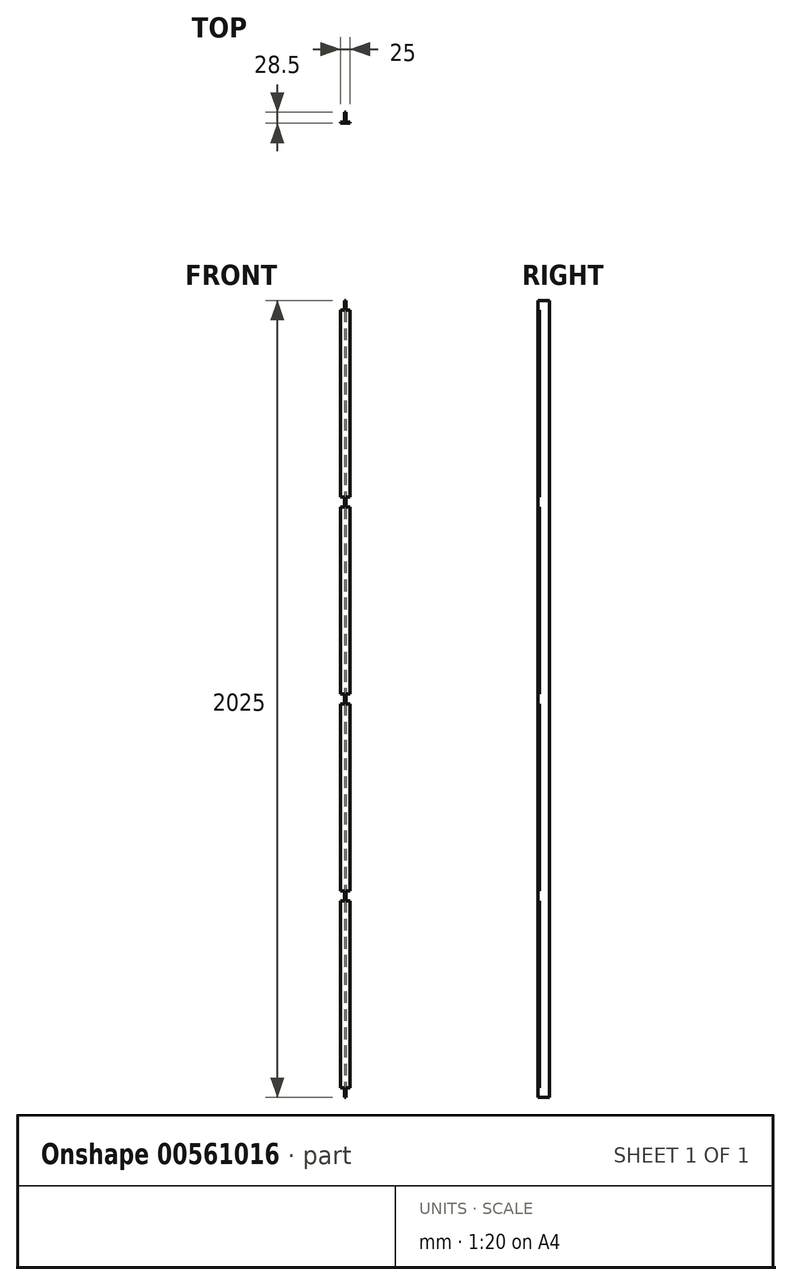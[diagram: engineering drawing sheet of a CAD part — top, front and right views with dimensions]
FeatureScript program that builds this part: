
annotation { "Feature Type Name" : "Feature", "Feature Type Description" : "" }
export const myFeature = defineFeature(function(context is Context, id is Id, definition is map)
    precondition{}
    {
        {
            var Q0;
            Q0=qCreatedBy(makeId("Top.planeOp"),FACE);
            var sketch = newSketch(context, id + "F0", { "sketchPlane" : qUnion([Q0])});
            skLineSegment(sketch, "E0", {"start": v(-14.25, -3.5) * mm, "end": v(10.75, -3.5) * mm});
            skLineSegment(sketch, "E1", {"start": v(10.75, -3.5) * mm, "end": v(10.75, 0) * mm});
            skLineSegment(sketch, "E2", {"start": v(10.75, 0) * mm, "end": v(0, 0) * mm});
            skLineSegment(sketch, "E3", {"start": v(0, 0) * mm, "end": v(0, 25) * mm});
            skLineSegment(sketch, "E4", {"start": v(0, 25) * mm, "end": v(-3.5, 25) * mm});
            skLineSegment(sketch, "E5", {"start": v(-3.5, 25) * mm, "end": v(-3.5, 0) * mm});
            skLineSegment(sketch, "E6", {"start": v(-14.25, 0) * mm, "end": v(-14.25, -3.5) * mm});
            skLineSegment(sketch, "E7", {"start": v(-3.5, 0) * mm, "end": v(-14.25, 0) * mm});
            skSolve(sketch);
        }
        {
            var Q0;
            Q0 = qSketchRegion(id + "F0", true);
            extrude(context, id + "F1", {"entities" : qUnion([Q0]), "depth" : 2025 * mm, "offsetDistance" : 25 * mm});
        }
        {
            var Q0;
            Q0=makeQuery(id+"F1.opExtrude","SWEPT_FACE",FACE,{"disambiguationData":[OSD([sQuery(id+"F0.wireOp",EDGE,"E7")])]});
            var sketch = newSketch(context, id + "F2", { "sketchPlane" : qUnion([Q0])});
            skLineSegment(sketch, "E8.bottom", {"start": v(14.25, 0) * mm, "end": v(3.5, 0) * mm});
            skLineSegment(sketch, "E8.top", {"start": v(14.25, 25) * mm, "end": v(3.5, 25) * mm});
            skLineSegment(sketch, "E8.left", {"start": v(14.25, 0) * mm, "end": v(14.25, 25) * mm});
            skLineSegment(sketch, "E8.right", {"start": v(3.5, 0) * mm, "end": v(3.5, 25) * mm});
            skLineSegment(sketch, "E9.bottom", {"start": v(0, 0) * mm, "end": v(-10.75, 0) * mm});
            skLineSegment(sketch, "E9.top", {"start": v(0, 25) * mm, "end": v(-10.75, 25) * mm});
            skLineSegment(sketch, "E9.left", {"start": v(0, 0) * mm, "end": v(0, 25) * mm});
            skLineSegment(sketch, "E9.right", {"start": v(-10.75, 0) * mm, "end": v(-10.75, 25) * mm});
            skLineSegment(sketch, "E10.bottom", {"start": v(3.5, 2025) * mm, "end": v(14.25, 2025) * mm});
            skLineSegment(sketch, "E10.top", {"start": v(3.5, 2000) * mm, "end": v(14.25, 2000) * mm});
            skLineSegment(sketch, "E10.left", {"start": v(3.5, 2025) * mm, "end": v(3.5, 2000) * mm});
            skLineSegment(sketch, "E10.right", {"start": v(14.25, 2025) * mm, "end": v(14.25, 2000) * mm});
            skLineSegment(sketch, "E11.bottom", {"start": v(0, 2000) * mm, "end": v(-10.75, 2000) * mm});
            skLineSegment(sketch, "E11.top", {"start": v(0, 2025) * mm, "end": v(-10.75, 2025) * mm});
            skLineSegment(sketch, "E11.left", {"start": v(0, 2000) * mm, "end": v(0, 2025) * mm});
            skLineSegment(sketch, "E11.right", {"start": v(-10.75, 2000) * mm, "end": v(-10.75, 2025) * mm});
            skLineSegment(sketch, "E12.bottom", {"start": v(3.5, 1525) * mm, "end": v(14.25, 1525) * mm});
            skLineSegment(sketch, "E12.top", {"start": v(3.5, 1500) * mm, "end": v(14.25, 1500) * mm});
            skLineSegment(sketch, "E12.left", {"start": v(3.5, 1525) * mm, "end": v(3.5, 1500) * mm});
            skLineSegment(sketch, "E12.right", {"start": v(14.25, 1525) * mm, "end": v(14.25, 1500) * mm});
            skLineSegment(sketch, "E13.bottom", {"start": v(0, 1525) * mm, "end": v(-10.75, 1525) * mm});
            skLineSegment(sketch, "E13.top", {"start": v(0, 1500) * mm, "end": v(-10.75, 1500) * mm});
            skLineSegment(sketch, "E13.left", {"start": v(0, 1525) * mm, "end": v(0, 1500) * mm});
            skLineSegment(sketch, "E13.right", {"start": v(-10.75, 1525) * mm, "end": v(-10.75, 1500) * mm});
            skLineSegment(sketch, "E14.bottom", {"start": v(14.25, 1025) * mm, "end": v(3.5, 1025) * mm});
            skLineSegment(sketch, "E14.top", {"start": v(14.25, 1000) * mm, "end": v(3.5, 1000) * mm});
            skLineSegment(sketch, "E14.left", {"start": v(14.25, 1025) * mm, "end": v(14.25, 1000) * mm});
            skLineSegment(sketch, "E14.right", {"start": v(3.5, 1025) * mm, "end": v(3.5, 1000) * mm});
            skLineSegment(sketch, "E15.bottom", {"start": v(0, 1000) * mm, "end": v(-10.75, 1000) * mm});
            skLineSegment(sketch, "E15.top", {"start": v(0, 1025) * mm, "end": v(-10.75, 1025) * mm});
            skLineSegment(sketch, "E15.left", {"start": v(0, 1000) * mm, "end": v(0, 1025) * mm});
            skLineSegment(sketch, "E15.right", {"start": v(-10.75, 1000) * mm, "end": v(-10.75, 1025) * mm});
            skLineSegment(sketch, "E16", {"start": v(-10.75, 1012.5) * mm, "end": v(-10.75, 1512.5) * mm});
            skLineSegment(sketch, "E17", {"start": v(-10.75, 1512.5) * mm, "end": v(-10.75, 2012.5) * mm});
            skLineSegment(sketch, "E18.bottom", {"start": v(3.5, 525) * mm, "end": v(14.25, 525) * mm});
            skLineSegment(sketch, "E18.top", {"start": v(3.5, 500) * mm, "end": v(14.25, 500) * mm});
            skLineSegment(sketch, "E18.left", {"start": v(3.5, 525) * mm, "end": v(3.5, 500) * mm});
            skLineSegment(sketch, "E18.right", {"start": v(14.25, 525) * mm, "end": v(14.25, 500) * mm});
            skLineSegment(sketch, "E19.bottom", {"start": v(0, 525) * mm, "end": v(-10.75, 525) * mm});
            skLineSegment(sketch, "E19.top", {"start": v(0, 500) * mm, "end": v(-10.75, 500) * mm});
            skLineSegment(sketch, "E19.left", {"start": v(0, 525) * mm, "end": v(0, 500) * mm});
            skLineSegment(sketch, "E19.right", {"start": v(-10.75, 525) * mm, "end": v(-10.75, 500) * mm});
            skLineSegment(sketch, "E20", {"start": v(-10.75, 1012.5) * mm, "end": v(-10.75, 512.5) * mm});
            skLineSegment(sketch, "E21", {"start": v(-10.75, 512.5) * mm, "end": v(-10.75, 12.5) * mm});
            skSolve(sketch);
        }
        {
            var Q0;
            Q0 = qSketchRegion(id + "F2", true);
            extrude(context, id + "F3", {"entities" : qUnion([Q0]), "operationType" : NewBodyOperationType.REMOVE, "endBound" : BoundingType.THROUGH_ALL, "oppositeDirection" : true, "depth" : 25 * mm, "offsetDistance" : 25 * mm});
        }
    });
